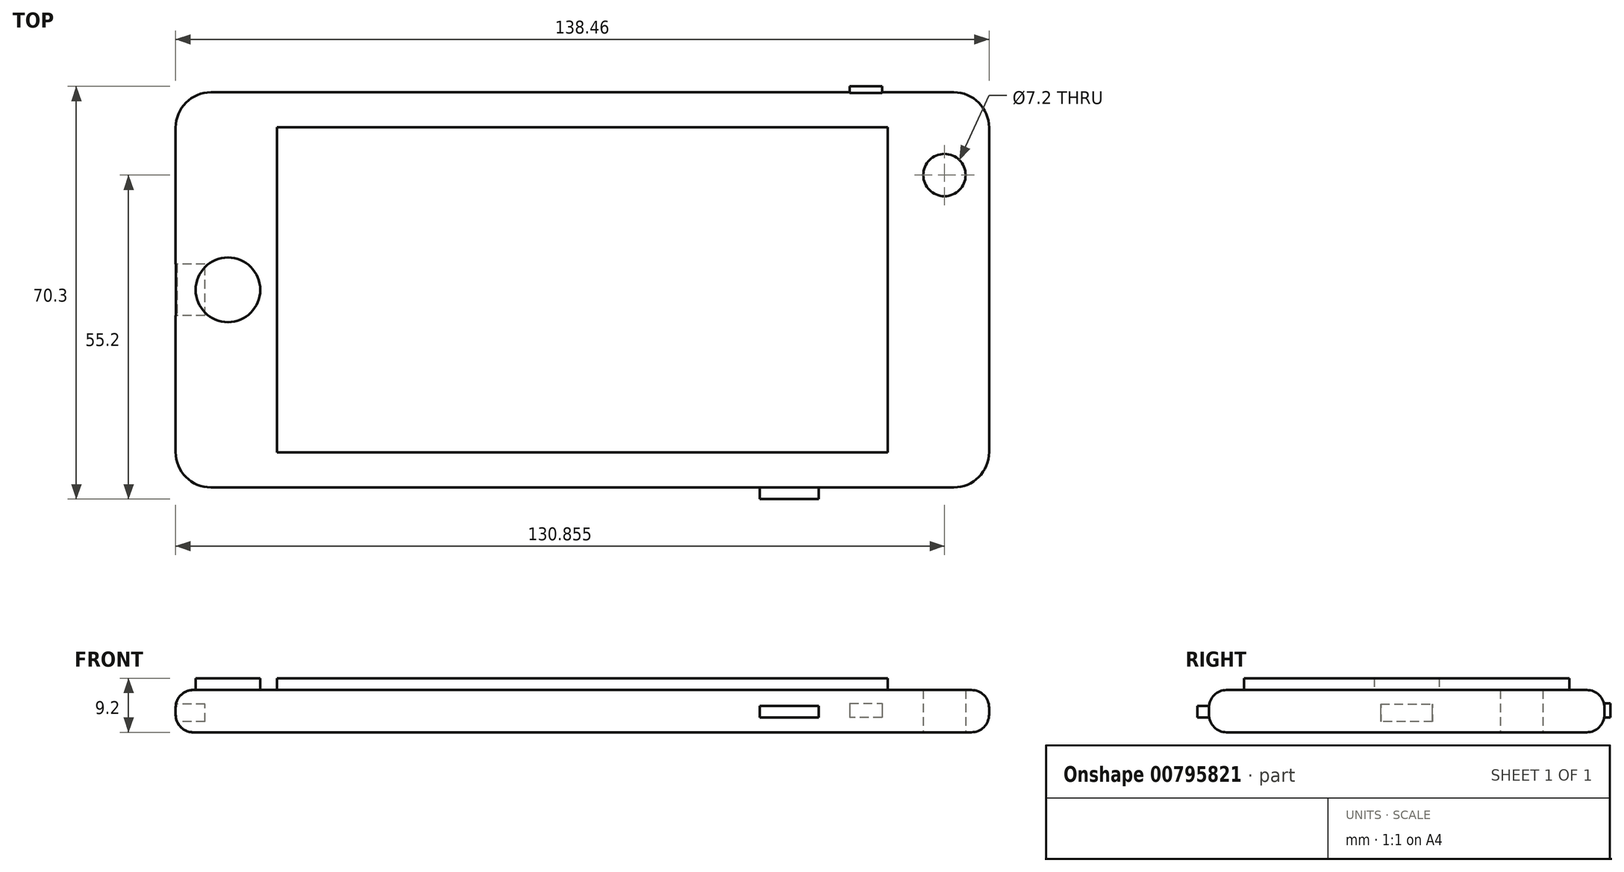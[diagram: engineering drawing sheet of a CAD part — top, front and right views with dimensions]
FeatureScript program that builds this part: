
annotation { "Feature Type Name" : "Feature", "Feature Type Description" : "" }
export const myFeature = defineFeature(function(context is Context, id is Id, definition is map)
    precondition{}
    {
        {
            var Q0;
            Q0=qCreatedBy(makeId("Top.planeOp"),FACE);
            var sketch = newSketch(context, id + "F0", { "sketchPlane" : qUnion([Q0])});
            skLineSegment(sketch, "E0.bottom", {"start": v(-63.22, 33.65) * mm, "end": v(63.23, 33.65) * mm});
            skLineSegment(sketch, "E0.top", {"start": v(-63.22, -33.65) * mm, "end": v(63.23, -33.65) * mm});
            skLineSegment(sketch, "E0.left", {"start": v(-69.22, 27.65) * mm, "end": v(-69.22, -27.65) * mm});
            skLineSegment(sketch, "E0.right", {"start": v(69.22, 27.65) * mm, "end": v(69.22, -27.65) * mm});
            skPoint(sketch, "E0.middle", {"position": v(0, 0) * mm});
            skPoint(sketch, "E1.visualSharp", {"position": v(-69.22, 33.65) * mm});
            skArc(sketch, "E1.filletArc", {"start": v(-63.22, 33.65) * mm, "mid": v(-67.47, 31.9) * mm, "end": v(-69.22, 27.65) * mm});
            skPoint(sketch, "E2.visualSharp", {"position": v(-69.22, -33.65) * mm});
            skArc(sketch, "E2.filletArc", {"start": v(-69.22, -27.65) * mm, "mid": v(-67.47, -31.9) * mm, "end": v(-63.22, -33.65) * mm});
            skPoint(sketch, "E3.visualSharp", {"position": v(69.22, -33.65) * mm});
            skArc(sketch, "E3.filletArc", {"start": v(63.23, -33.65) * mm, "mid": v(67.47, -31.9) * mm, "end": v(69.23, -27.65) * mm});
            skPoint(sketch, "E4.visualSharp", {"position": v(69.23, 33.65) * mm});
            skArc(sketch, "E4.filletArc", {"start": v(69.23, 27.65) * mm, "mid": v(67.47, 31.9) * mm, "end": v(63.23, 33.65) * mm});
            skLineSegment(sketch, "E5", {"start": v(69.23, 19.55) * mm, "end": v(61.63, 19.55) * mm, "construction": true});
            skPoint(sketch, "E6", {"position": v(61.63, 19.55) * mm});
            skCircle(sketch, "E7", {"center": v(61.63, 19.55) * mm, "radius": 3.6 * mm});
            skSolve(sketch);
        }
        {
            var Q0;
            Q0=makeQuery(id+"F0.imprint","IMPRINT",FACE,{"disambiguationData":[TD([[makeQuery(id+"F0.imprint","IMPRINT",EDGE,{"derivedFrom":sQuery(id+"F0.wireOp",EDGE,"E0.bottom")}),-1.0]])]});
            extrude(context, id + "F1", {"entities" : qUnion([Q0]), "depth" : 7.2 * mm, "offsetDistance" : 25 * mm});
        }
        {
            var Q0;
            Q0=makeQuery(id+"F1.opExtrude","SWEPT_FACE",FACE,{"disambiguationData":[OSD([sQuery(id+"F0.wireOp",EDGE,"E0.bottom")])]});
            var sketch = newSketch(context, id + "F2", { "sketchPlane" : qUnion([Q0])});
            skLineSegment(sketch, "E8.bottom", {"start": v(-45.53, 4.93) * mm, "end": v(-51.03, 4.93) * mm});
            skLineSegment(sketch, "E8.top", {"start": v(-45.53, 2.53) * mm, "end": v(-51.03, 2.53) * mm});
            skLineSegment(sketch, "E8.left", {"start": v(-45.53, 4.93) * mm, "end": v(-45.53, 2.53) * mm});
            skLineSegment(sketch, "E8.right", {"start": v(-51.03, 4.93) * mm, "end": v(-51.03, 2.53) * mm});
            skPoint(sketch, "E8.middle", {"position": v(-48.28, 3.73) * mm});
            skSolve(sketch);
        }
        {
            var Q0;
            Q0=makeQuery(id+"F2.imprint","IMPRINT",FACE,{"disambiguationData":[TD([[makeQuery(id+"F2.imprint","IMPRINT",EDGE,{"derivedFrom":sQuery(id+"F2.wireOp",EDGE,"E8.bottom")}),1.0]])]});
            extrude(context, id + "F3", {"entities" : qUnion([Q0]), "operationType" : NewBodyOperationType.ADD, "depth" : 1 * mm, "offsetDistance" : 25 * mm});
        }
        {
            var Q0;
            Q0=makeQuery(id+"F1.opExtrude","SWEPT_FACE",FACE,{"disambiguationData":[OSD([sQuery(id+"F0.wireOp",EDGE,"E0.top")])]});
            var sketch = newSketch(context, id + "F4", { "sketchPlane" : qUnion([Q0])});
            skLineSegment(sketch, "E9.bottom", {"start": v(40.22, 2.5) * mm, "end": v(30.22, 2.5) * mm});
            skLineSegment(sketch, "E9.top", {"start": v(40.22, 4.5) * mm, "end": v(30.22, 4.5) * mm});
            skLineSegment(sketch, "E9.left", {"start": v(40.22, 2.5) * mm, "end": v(40.22, 4.5) * mm});
            skLineSegment(sketch, "E9.right", {"start": v(30.22, 2.5) * mm, "end": v(30.22, 4.5) * mm});
            skPoint(sketch, "E9.middle", {"position": v(35.22, 3.5) * mm});
            skSolve(sketch);
        }
        {
            var Q0;
            Q0=makeQuery(id+"F4.imprint","IMPRINT",FACE,{"disambiguationData":[TD([[makeQuery(id+"F4.imprint","IMPRINT",EDGE,{"derivedFrom":sQuery(id+"F4.wireOp",EDGE,"E9.bottom")}),-1.0]])]});
            extrude(context, id + "F5", {"entities" : qUnion([Q0]), "operationType" : NewBodyOperationType.ADD, "depth" : 2 * mm, "offsetDistance" : 25 * mm});
        }
        {
            var Q0;
            Q0=makeQuery(id+"F1.opExtrude","SWEPT_FACE",FACE,{"disambiguationData":[OSD([sQuery(id+"F0.wireOp",EDGE,"E0.left")])]});
            var sketch = newSketch(context, id + "F6", { "sketchPlane" : qUnion([Q0])});
            skLineSegment(sketch, "E10.bottom", {"start": v(4.4, 1.8) * mm, "end": v(-4.4, 1.8) * mm});
            skLineSegment(sketch, "E10.top", {"start": v(4.4, 4.8) * mm, "end": v(-4.4, 4.8) * mm});
            skLineSegment(sketch, "E10.left", {"start": v(4.4, 1.8) * mm, "end": v(4.4, 4.8) * mm});
            skLineSegment(sketch, "E10.right", {"start": v(-4.4, 1.8) * mm, "end": v(-4.4, 4.8) * mm});
            skPoint(sketch, "E10.middle", {"position": v(0, 3.3) * mm});
            skSolve(sketch);
        }
        {
            var Q0;
            Q0=makeQuery(id+"F6.imprint","IMPRINT",FACE,{"disambiguationData":[TD([[makeQuery(id+"F6.imprint","IMPRINT",EDGE,{"derivedFrom":sQuery(id+"F6.wireOp",EDGE,"E10.bottom")}),-1.0]])]});
            extrude(context, id + "F7", {"entities" : qUnion([Q0]), "operationType" : NewBodyOperationType.REMOVE, "oppositeDirection" : true, "depth" : 5 * mm, "offsetDistance" : 25 * mm});
        }
        {
            var Q0;
            Q0=makeQuery(id+"F1.opExtrude","CAP_FACE",FACE,{"disambiguationData":[OSD([sQuery(id+"F0.wireOp",EDGE,"E0.bottom"),sQuery(id+"F0.wireOp",EDGE,"E0.top"),sQuery(id+"F0.wireOp",EDGE,"E0.left"),sQuery(id+"F0.wireOp",EDGE,"E0.right"),sQuery(id+"F0.wireOp",EDGE,"E1.filletArc"),sQuery(id+"F0.wireOp",EDGE,"E2.filletArc"),sQuery(id+"F0.wireOp",EDGE,"E3.filletArc"),sQuery(id+"F0.wireOp",EDGE,"E4.filletArc"),sQuery(id+"F0.wireOp",EDGE,"E7")])],"isStart":false});
            var sketch = newSketch(context, id + "F8", { "sketchPlane" : qUnion([Q0])});
            skLineSegment(sketch, "E11", {"start": v(-69.22, 0) * mm, "end": v(-60.32, 0) * mm, "construction": true});
            skCircle(sketch, "E12", {"center": v(-60.32, 0) * mm, "radius": 5.5 * mm});
            skSolve(sketch);
        }
        {
            var Q0;
            Q0=makeQuery(id+"F8.imprint","IMPRINT",FACE,{"disambiguationData":[TD([[makeQuery(id+"F8.imprint","IMPRINT",EDGE,{"derivedFrom":sQuery(id+"F8.wireOp",EDGE,"E12")}),1.0]])]});
            extrude(context, id + "F9", {"entities" : qUnion([Q0]), "operationType" : NewBodyOperationType.ADD, "depth" : 2 * mm, "offsetDistance" : 25 * mm});
        }
        {
            var Q0;
            Q0=makeQuery(id+"F1.opExtrude","CAP_FACE",FACE,{"disambiguationData":[OSD([sQuery(id+"F0.wireOp",EDGE,"E0.bottom"),sQuery(id+"F0.wireOp",EDGE,"E0.top"),sQuery(id+"F0.wireOp",EDGE,"E0.left"),sQuery(id+"F0.wireOp",EDGE,"E0.right"),sQuery(id+"F0.wireOp",EDGE,"E1.filletArc"),sQuery(id+"F0.wireOp",EDGE,"E2.filletArc"),sQuery(id+"F0.wireOp",EDGE,"E3.filletArc"),sQuery(id+"F0.wireOp",EDGE,"E4.filletArc"),sQuery(id+"F0.wireOp",EDGE,"E7")])],"isStart":false});
            var sketch = newSketch(context, id + "F10", { "sketchPlane" : qUnion([Q0])});
            skLineSegment(sketch, "E13.bottom", {"start": v(51.95, 27.67) * mm, "end": v(-51.95, 27.67) * mm});
            skLineSegment(sketch, "E13.top", {"start": v(51.95, -27.66) * mm, "end": v(-51.95, -27.66) * mm});
            skLineSegment(sketch, "E13.left", {"start": v(51.95, 27.67) * mm, "end": v(51.95, -27.66) * mm});
            skLineSegment(sketch, "E13.right", {"start": v(-51.95, 27.67) * mm, "end": v(-51.95, -27.66) * mm});
            skPoint(sketch, "E13.middle", {"position": v(0, 0) * mm});
            skSolve(sketch);
        }
        {
            var Q0;
            Q0=makeQuery(id+"F10.imprint","IMPRINT",FACE,{"disambiguationData":[TD([[makeQuery(id+"F10.imprint","IMPRINT",EDGE,{"derivedFrom":sQuery(id+"F10.wireOp",EDGE,"E13.bottom")}),1.0]])]});
            extrude(context, id + "F11", {"entities" : qUnion([Q0]), "operationType" : NewBodyOperationType.ADD, "depth" : 2 * mm, "offsetDistance" : 25 * mm});
        }
        {
            var Q0;
            Q0=makeQuery(id+"F1.opExtrude","CAP_EDGE",EDGE,{"disambiguationData":[OSD([sQuery(id+"F0.wireOp",EDGE,"E0.bottom")])],"isStart":false});
            var Q1;
            Q1=makeQuery(id+"F1.opExtrude","CAP_EDGE",EDGE,{"disambiguationData":[OSD([sQuery(id+"F0.wireOp",EDGE,"E1.filletArc")])],"isStart":false});
            var Q2;
            Q2=makeQuery(id+"F1.opExtrude","CAP_EDGE",EDGE,{"disambiguationData":[OSD([sQuery(id+"F0.wireOp",EDGE,"E0.left")])],"isStart":false});
            var Q3;
            Q3=makeQuery(id+"F1.opExtrude","CAP_EDGE",EDGE,{"disambiguationData":[OSD([sQuery(id+"F0.wireOp",EDGE,"E0.top")])],"isStart":false});
            var Q4;
            Q4=makeQuery(id+"F1.opExtrude","CAP_EDGE",EDGE,{"disambiguationData":[OSD([sQuery(id+"F0.wireOp",EDGE,"E2.filletArc")])],"isStart":false});
            var Q5;
            Q5=makeQuery(id+"F1.opExtrude","CAP_EDGE",EDGE,{"disambiguationData":[OSD([sQuery(id+"F0.wireOp",EDGE,"E3.filletArc")])],"isStart":false});
            var Q6;
            Q6=makeQuery(id+"F1.opExtrude","CAP_EDGE",EDGE,{"disambiguationData":[OSD([sQuery(id+"F0.wireOp",EDGE,"E0.right")])],"isStart":false});
            var Q7;
            Q7=makeQuery(id+"F1.opExtrude","CAP_EDGE",EDGE,{"disambiguationData":[OSD([sQuery(id+"F0.wireOp",EDGE,"E4.filletArc")])],"isStart":false});
            fillet(context, id + "F12", {"entities" : qUnion([Q0, Q1, Q2, Q3, Q4, Q5, Q6, Q7]), "radius" : 3 * mm, "tangentPropagation" : true, "allowEdgeOverflow" : false});
        }
        {
            var Q0;
            Q0=makeQuery(id+"F1.opExtrude","CAP_EDGE",EDGE,{"disambiguationData":[OSD([sQuery(id+"F0.wireOp",EDGE,"E0.left")])],"isStart":true});
            var Q1;
            Q1=makeQuery(id+"F1.opExtrude","CAP_EDGE",EDGE,{"disambiguationData":[OSD([sQuery(id+"F0.wireOp",EDGE,"E0.top")])],"isStart":true});
            var Q2;
            Q2=makeQuery(id+"F1.opExtrude","CAP_EDGE",EDGE,{"disambiguationData":[OSD([sQuery(id+"F0.wireOp",EDGE,"E2.filletArc")])],"isStart":true});
            var Q3;
            Q3=makeQuery(id+"F1.opExtrude","CAP_EDGE",EDGE,{"disambiguationData":[OSD([sQuery(id+"F0.wireOp",EDGE,"E1.filletArc")])],"isStart":true});
            var Q4;
            Q4=makeQuery(id+"F1.opExtrude","CAP_EDGE",EDGE,{"disambiguationData":[OSD([sQuery(id+"F0.wireOp",EDGE,"E0.bottom")])],"isStart":true});
            var Q5;
            Q5=makeQuery(id+"F1.opExtrude","CAP_EDGE",EDGE,{"disambiguationData":[OSD([sQuery(id+"F0.wireOp",EDGE,"E0.right")])],"isStart":true});
            var Q6;
            Q6=makeQuery(id+"F1.opExtrude","CAP_EDGE",EDGE,{"disambiguationData":[OSD([sQuery(id+"F0.wireOp",EDGE,"E4.filletArc")])],"isStart":true});
            var Q7;
            Q7=makeQuery(id+"F1.opExtrude","CAP_EDGE",EDGE,{"disambiguationData":[OSD([sQuery(id+"F0.wireOp",EDGE,"E3.filletArc")])],"isStart":true});
            fillet(context, id + "F13", {"entities" : qUnion([Q0, Q1, Q2, Q3, Q4, Q5, Q6, Q7]), "radius" : 3 * mm, "tangentPropagation" : true, "allowEdgeOverflow" : false});
        }
    });
